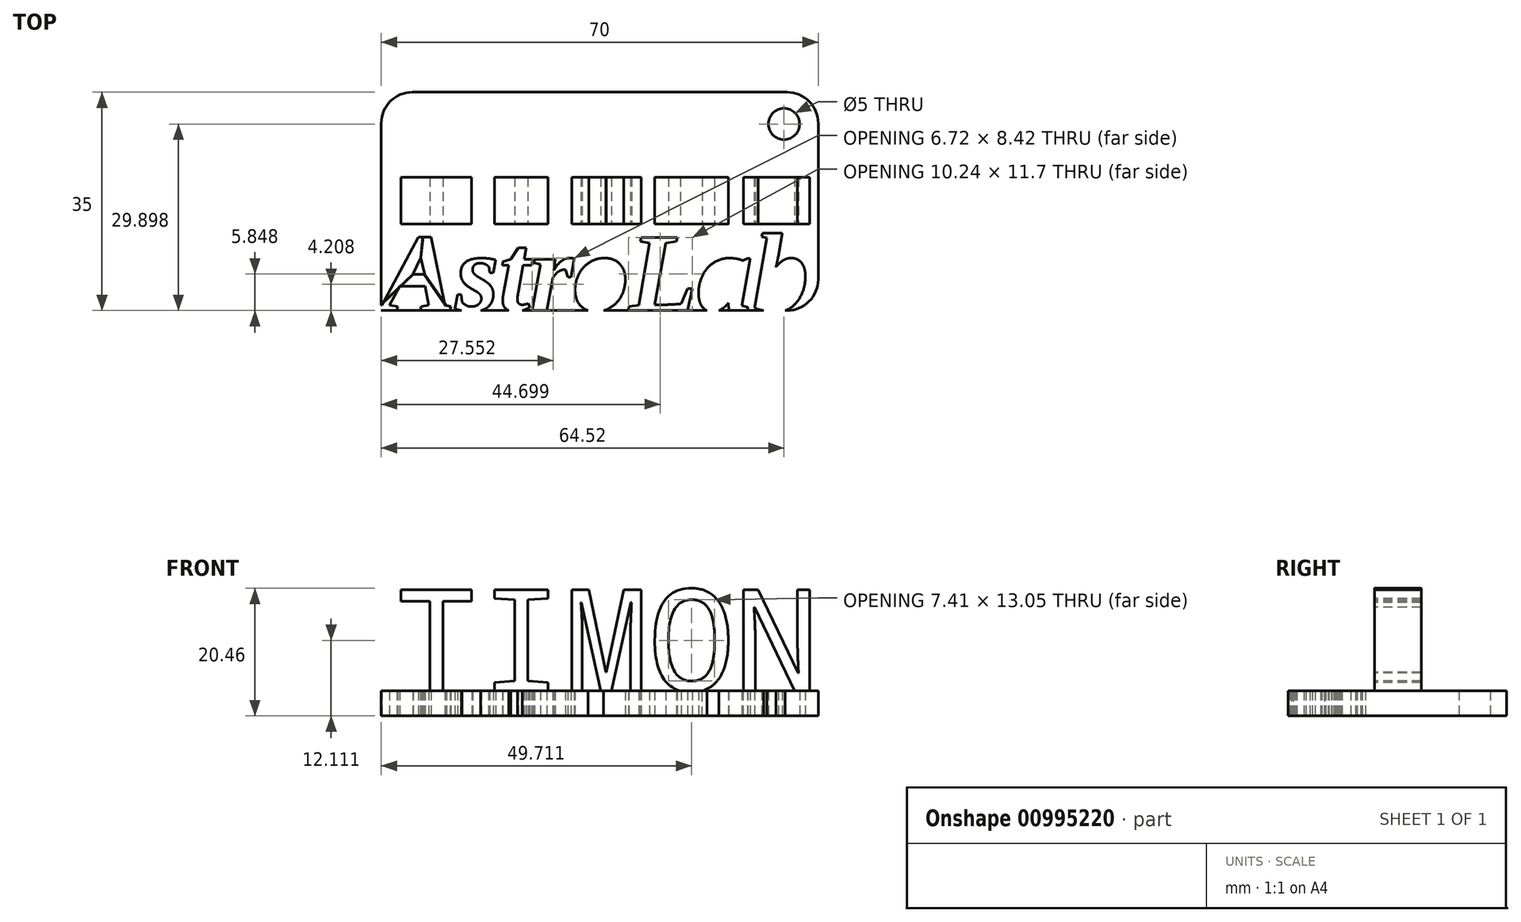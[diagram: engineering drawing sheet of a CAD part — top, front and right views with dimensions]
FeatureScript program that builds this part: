
annotation { "Feature Type Name" : "Feature", "Feature Type Description" : "" }
export const myFeature = defineFeature(function(context is Context, id is Id, definition is map)
    precondition{}
    {
        {
            var Q0;
            Q0=qCreatedBy(makeId("Top.planeOp"),FACE);
            var Q1;
            Q1=qCreatedBy(makeId("Top.planeOp"),FACE);
            var sketch = newSketch(context, id + "F0", { "sketchPlane" : qUnion([Q0, Q1])});
            skLineSegment(sketch, "E0.bottom", {"start": v(-37.03, 21.16) * mm, "end": v(32.97, 21.16) * mm});
            skLineSegment(sketch, "E0.top", {"start": v(-37.03, -13.84) * mm, "end": v(32.97, -13.84) * mm});
            skLineSegment(sketch, "E0.left", {"start": v(-37.03, 21.16) * mm, "end": v(-37.03, -13.84) * mm});
            skLineSegment(sketch, "E0.right", {"start": v(32.97, 21.16) * mm, "end": v(32.97, -13.84) * mm});
            skText(sketch, "E1", { "text": "AstroLab", "fontName": "Tinos-BoldItalic.ttf"});
            skCircle(sketch, "E2", {"center": v(27.49, 16.06) * mm, "radius": 2.5 * mm});
            const initialGuessF0  = {"E1": [-0.03703, -0.01384, 1, 0, 0.01286]};
            skSetInitialGuess(sketch, initialGuessF0);
            skSolve(sketch);
        }
        {
            var Q0;
            Q0=makeQuery(id+"F0.imprint","IMPRINT",FACE,{"disambiguationData":[TD([[makeQuery(id+"F0.imprint","IMPRINT",EDGE,{"derivedFrom":sQuery(id+"F0.wireOp",EDGE,"E0.bottom")}),-1.0]])]});
            extrude(context, id + "F1", {"entities" : qUnion([Q0]), "depth" : 4 * mm, "offsetDistance" : 25 * mm});
        }
        {
            var Q0;
            Q0=qCreatedBy(makeId("Front.planeOp"),FACE);
            var sketch = newSketch(context, id + "F2", { "sketchPlane" : qUnion([Q0])});
            skText(sketch, "E3", { "text": "TIMON", "fontName": "DroidSansMono.ttf"});
            const initialGuessF2  = {"E3": [-0.035, 0.004, 1, 0, 0.01634]};
            skSetInitialGuess(sketch, initialGuessF2);
            skSolve(sketch);
        }
        {
            var Q0;
            Q0 = qSketchRegion(id + "F2", true);
            extrude(context, id + "F3", {"entities" : qUnion([Q0]), "operationType" : NewBodyOperationType.ADD, "oppositeDirection" : true, "depth" : 7.5 * mm, "offsetDistance" : 25 * mm});
        }
        {
            var Q0;
            Q0=qCreatedBy(makeId("Top.planeOp"),FACE);
            var sketch = newSketch(context, id + "F4", { "sketchPlane" : qUnion([Q0])});
            skLineSegment(sketch, "E4", {"start": v(-31.95, -8.03) * mm, "end": v(-30.7, -5.35) * mm});
            skLineSegment(sketch, "E5", {"start": v(-30.7, -5.35) * mm, "end": v(-30.09, -8.03) * mm});
            skLineSegment(sketch, "E6", {"start": v(-31.95, -8.03) * mm, "end": v(-30.09, -8.03) * mm});
            skLineSegment(sketch, "E7", {"start": v(-31.95, -8.03) * mm, "end": v(-36.89, -12.73) * mm});
            skLineSegment(sketch, "E8", {"start": v(-30.09, -8.03) * mm, "end": v(-26.6, -13.06) * mm});
            skLineSegment(sketch, "E9", {"start": v(-30.2, -8.03) * mm, "end": v(-26.8, -12.91) * mm});
            skLineSegment(sketch, "E10", {"start": v(-26.8, -12.91) * mm, "end": v(-26.6, -13.06) * mm});
            skLineSegment(sketch, "E11", {"start": v(-31.88, -8.03) * mm, "end": v(-36.89, -12.8) * mm});
            skLineSegment(sketch, "E12", {"start": v(-36.89, -12.8) * mm, "end": v(-36.89, -12.73) * mm});
            skLineSegment(sketch, "E13", {"start": v(-30.7, -5.35) * mm, "end": v(-30.4, -1.98) * mm});
            skLineSegment(sketch, "E14", {"start": v(-30.68, -5.42) * mm, "end": v(-30.34, -2.05) * mm});
            skLineSegment(sketch, "E15", {"start": v(-30.4, -1.98) * mm, "end": v(-30.34, -2.05) * mm});
            skSolve(sketch);
        }
        {
            var Q0;
            Q0=makeQuery(id+"F4.imprint","IMPRINT",FACE,{"disambiguationData":[TD([[makeQuery(id+"F4.imprint","IMPRINT",EDGE,{"derivedFrom":sQuery(id+"F4.wireOp",EDGE,"E4")}),-1.0]])]});
            extrude(context, id + "F5", {"entities" : qUnion([Q0]), "depth" : 4 * mm, "offsetDistance" : 25 * mm});
        }
        {
            var Q0;
            Q0 = qSketchRegion(id + "F4", true);
            extrude(context, id + "F6", {"entities" : qUnion([Q0]), "depth" : 4 * mm, "offsetDistance" : 25 * mm});
        }
        {
            var Q0;
            Q0=makeQuery(id+"F1.opExtrude","SWEPT_EDGE",EDGE,{"disambiguationData":[OSD([sQuery(id+"F0.wireOp",EDGE,"E0.top"),sQuery(id+"F0.wireOp",EDGE,"E0.right")])]});
            var Q1;
            Q1=makeQuery(id+"F1.opExtrude","SWEPT_EDGE",EDGE,{"disambiguationData":[OSD([sQuery(id+"F0.wireOp",EDGE,"E0.bottom"),sQuery(id+"F0.wireOp",EDGE,"E0.right")])]});
            var Q2;
            Q2=makeQuery(id+"F1.opExtrude","SWEPT_EDGE",EDGE,{"disambiguationData":[OSD([sQuery(id+"F0.wireOp",EDGE,"E0.bottom"),sQuery(id+"F0.wireOp",EDGE,"E0.left")])]});
            fillet(context, id + "F7", {"entities" : qUnion([Q0, Q1, Q2]), "radius" : 5 * mm, "tangentPropagation" : true, "allowEdgeOverflow" : false});
        }
    });
